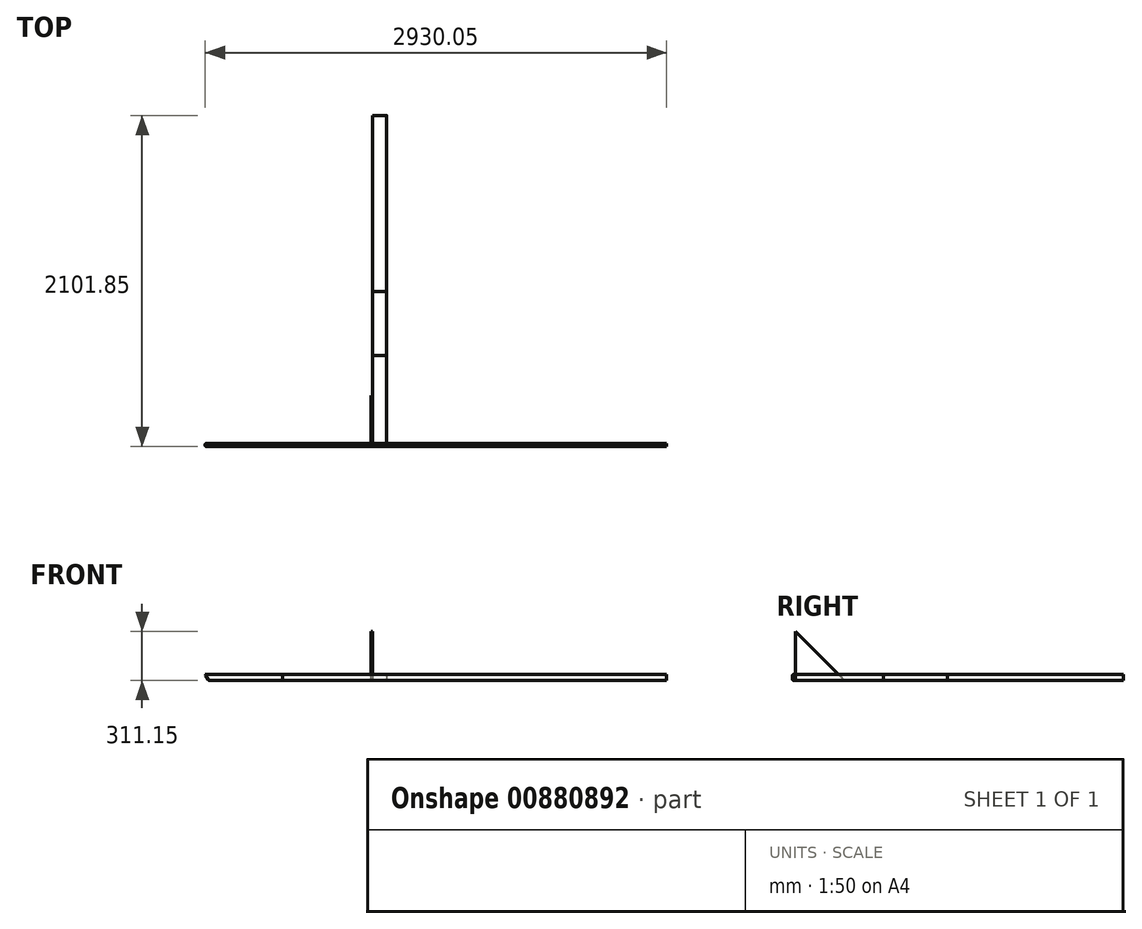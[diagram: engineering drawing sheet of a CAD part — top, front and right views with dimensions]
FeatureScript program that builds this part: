
annotation { "Feature Type Name" : "Feature", "Feature Type Description" : "" }
export const myFeature = defineFeature(function(context is Context, id is Id, definition is map)
    precondition{}
    {
        {
            var Q0;
            Q0=qCreatedBy(makeId("Top.planeOp"),FACE);
            var sketch = newSketch(context, id + "F0", { "sketchPlane" : qUnion([Q0])});
            skLineSegment(sketch, "E0", {"start": v(-1219.2, -1219.2) * mm, "end": v(0, 0) * mm});
            skLineSegment(sketch, "E1", {"start": v(0, 0) * mm, "end": v(1219.2, -1219.2) * mm});
            skLineSegment(sketch, "E2", {"start": v(1219.2, -1219.2) * mm, "end": v(-1219.2, -1219.2) * mm});
            skLineSegment(sketch, "E3", {"start": v(-1219.2, -1219.2) * mm, "end": v(-1219.2, -1238.25) * mm});
            skLineSegment(sketch, "E4", {"start": v(-1219.2, -1238.25) * mm, "end": v(1219.2, -1238.25) * mm});
            skLineSegment(sketch, "E5", {"start": v(1219.2, -1238.25) * mm, "end": v(1219.2, -1219.2) * mm});
            skLineSegment(sketch, "E6.bottom", {"start": v(-558.8, -1219.2) * mm, "end": v(-647.7, -1219.2) * mm});
            skLineSegment(sketch, "E6.top", {"start": v(-558.8, -660.4) * mm, "end": v(-647.7, -660.4) * mm});
            skLineSegment(sketch, "E6.left", {"start": v(-558.8, -1219.2) * mm, "end": v(-558.8, -660.4) * mm});
            skLineSegment(sketch, "E6.right", {"start": v(-647.7, -1219.2) * mm, "end": v(-647.7, -660.4) * mm});
            skLineSegment(sketch, "E7.bottom", {"start": v(558.8, -1219.2) * mm, "end": v(647.7, -1219.2) * mm});
            skLineSegment(sketch, "E7.top", {"start": v(558.8, -660.4) * mm, "end": v(647.7, -660.4) * mm});
            skLineSegment(sketch, "E7.left", {"start": v(558.8, -1219.2) * mm, "end": v(558.8, -660.4) * mm});
            skLineSegment(sketch, "E7.right", {"start": v(647.7, -1219.2) * mm, "end": v(647.7, -660.4) * mm});
            skLineSegment(sketch, "E8", {"start": v(-558.8, -660.4) * mm, "end": v(558.8, -660.4) * mm});
            skLineSegment(sketch, "E9", {"start": v(0, -660.4) * mm, "end": v(0, 0) * mm});
            skSolve(sketch);
        }
        {
            var Q0;
            {var subQ5=sQuery(id+"F0.wireOp",EDGE,"E3");Q0=makeQuery(id+"F0.imprint","IMPRINT",FACE,{"disambiguationData":[TD([[makeQuery(id+"F0.imprint","IMPRINT",EDGE,{"derivedFrom":subQ5}),1.0]])]});}
            extrude(context, id + "F1", {"entities" : qUnion([Q0]), "depth" : 38.1 * mm, "offsetDistance" : 25.4 * mm});
        }
        {
            var Q0;
            Q0=makeQuery(id+"F1.opExtrude","CAP_EDGE",EDGE,{"disambiguationData":[OSD([sQuery(id+"F0.wireOp",EDGE,"E4")])],"isStart":false});
            var Q1;
            Q1=makeQuery(id+"F1.opExtrude","CAP_EDGE",EDGE,{"disambiguationData":[OSD([sQuery(id+"F0.wireOp",EDGE,"E2")])],"isStart":false});
            var Q2;
            Q2=makeQuery(id+"F1.opExtrude","CAP_EDGE",EDGE,{"disambiguationData":[OSD([sQuery(id+"F0.wireOp",EDGE,"E4")])],"isStart":true});
            var Q3;
            Q3=makeQuery(id+"F1.opExtrude","CAP_EDGE",EDGE,{"disambiguationData":[OSD([sQuery(id+"F0.wireOp",EDGE,"E2")])],"isStart":true});
            fillet(context, id + "F2", {"entities" : qUnion([Q0, Q1, Q2, Q3]), "radius" : 6.35 * mm, "tangentPropagation" : true, "allowEdgeOverflow" : false});
        }
        {
            var Q0;
            Q0=makeQuery(id+"F1.opExtrude","SWEPT_FACE",FACE,{"disambiguationData":[OSD([sQuery(id+"F0.wireOp",EDGE,"E4")])]});
            var sketch = newSketch(context, id + "F3", { "sketchPlane" : qUnion([Q0])});
            skLineSegment(sketch, "E10", {"start": v(1173.07, 38.1) * mm, "end": v(1195.07, 0) * mm});
            skLineSegment(sketch, "E11", {"start": v(1195.07, 0) * mm, "end": v(703.42, 0) * mm});
            skLineSegment(sketch, "E12", {"start": v(703.42, 0) * mm, "end": v(703.42, 38.1) * mm});
            skLineSegment(sketch, "E13", {"start": v(703.42, 38.1) * mm, "end": v(211.76, 38.1) * mm});
            skLineSegment(sketch, "E14", {"start": v(211.76, 38.1) * mm, "end": v(233.76, 0) * mm});
            skLineSegment(sketch, "E15", {"start": v(233.76, 0) * mm, "end": v(-257.9, 0) * mm});
            skLineSegment(sketch, "E16", {"start": v(-257.9, 0) * mm, "end": v(-257.9, 38.1) * mm});
            skLineSegment(sketch, "E17", {"start": v(-257.9, 38.1) * mm, "end": v(-749.54, 38.1) * mm});
            skLineSegment(sketch, "E18", {"start": v(-749.54, 38.1) * mm, "end": v(-727.55, 0) * mm});
            skLineSegment(sketch, "E19", {"start": v(-727.55, 0) * mm, "end": v(-1219.2, 0) * mm});
            skLineSegment(sketch, "E20", {"start": v(-1219.2, 0) * mm, "end": v(-1219.2, 38.1) * mm});
            skLineSegment(sketch, "E21", {"start": v(-1219.2, 38.1) * mm, "end": v(-1710.85, 38.1) * mm});
            skLineSegment(sketch, "E22", {"start": v(-1710.85, 38.1) * mm, "end": v(-1688.86, 0) * mm});
            skLineSegment(sketch, "E23", {"start": v(-1688.86, 0) * mm, "end": v(-1710.85, 0) * mm});
            skLineSegment(sketch, "E24", {"start": v(-1710.85, 0) * mm, "end": v(-1710.85, 38.1) * mm});
            skSolve(sketch);
        }
        {
            var Q0;
            Q0=makeQuery(id+"F1.opExtrude","SWEPT_FACE",FACE,{"disambiguationData":[OSD([sQuery(id+"F0.wireOp",EDGE,"E3")])]});
            var Q1;
            Q1=sQuery(id+"F3.wireOp",VERTEX,"E21.end");
            extrude(context, id + "F4", {"entities" : qUnion([Q0]), "endBound" : BoundingType.UP_TO_VERTEX, "depth" : 482.6 * mm, "endBoundEntityVertex" : qUnion([Q1]), "offsetDistance" : 25.4 * mm});
        }
        {
            var Q0;
            Q0=makeQuery(id+"F3.imprint","IMPRINT",FACE,{"disambiguationData":[TD([[makeQuery(id+"F3.imprint","IMPRINT",EDGE,{"derivedFrom":sQuery(id+"F3.wireOp",EDGE,"E22")}),-1.0]])]});
            extrude(context, id + "F5", {"entities" : qUnion([Q0]), "operationType" : NewBodyOperationType.REMOVE, "endBound" : BoundingType.THROUGH_ALL, "oppositeDirection" : true, "depth" : 25.4 * mm, "offsetDistance" : 25.4 * mm});
        }
        {
            var Q0;
            Q0=makeQuery(id+"F0.imprint","IMPRINT",FACE,{"disambiguationData":[TD([[makeQuery(id+"F0.imprint","IMPRINT",EDGE,{"derivedFrom":sQuery(id+"F0.wireOp",EDGE,"E6.top")}),1.0]])]});
            extrude(context, id + "F6", {"entities" : qUnion([Q0]), "depth" : 38.1 * mm, "offsetDistance" : 25.4 * mm});
        }
        {
            var Q0;
            Q0=makeQuery(id+"F6.opExtrude","CAP_EDGE",EDGE,{"disambiguationData":[OSD([sQuery(id+"F0.wireOp",EDGE,"E6.right")])],"isStart":false});
            var Q1;
            Q1=makeQuery(id+"F6.opExtrude","CAP_EDGE",EDGE,{"disambiguationData":[OSD([sQuery(id+"F0.wireOp",EDGE,"E6.right")])],"isStart":true});
            var Q2;
            Q2=makeQuery(id+"F6.opExtrude","CAP_EDGE",EDGE,{"disambiguationData":[OSD([sQuery(id+"F0.wireOp",EDGE,"E6.left")])],"isStart":false});
            var Q3;
            Q3=makeQuery(id+"F6.opExtrude","CAP_EDGE",EDGE,{"disambiguationData":[OSD([sQuery(id+"F0.wireOp",EDGE,"E6.left")])],"isStart":true});
            var Q4;
            Q4=makeQuery(id+"F5.boolean.opBoolean","COPY",EDGE,{"derivedFrom":makeQuery(id+"F5.opExtrude","CAP_EDGE",EDGE,{"disambiguationData":[OSD([sQuery(id+"F3.wireOp",EDGE,"E22")])],"isStart":true})});
            fillet(context, id + "F7", {"entities" : qUnion([Q0, Q1, Q2, Q3, Q4]), "radius" : 6.35 * mm, "tangentPropagation" : true, "allowEdgeOverflow" : false});
        }
        {
            var Q0;
            Q0=makeQuery(id+"F6.opExtrude","SWEPT_FACE",FACE,{"disambiguationData":[OSD([sQuery(id+"F0.wireOp",EDGE,"E6.top")])]});
            extrude(context, id + "F8", {"entities" : qUnion([Q0]), "depth" : 406.4 * mm, "offsetDistance" : 25.4 * mm});
        }
        {
            var Q0;
            Q0=makeQuery(id+"F6.opExtrude","SWEPT_FACE",FACE,{"disambiguationData":[OSD([sQuery(id+"F0.wireOp",EDGE,"E6.right")])]});
            var sketch = newSketch(context, id + "F9", { "sketchPlane" : qUnion([Q0])});
            skLineSegment(sketch, "E25", {"start": v(914.4, 6.35) * mm, "end": v(1219.2, 6.35) * mm});
            skLineSegment(sketch, "E26", {"start": v(1219.2, 6.35) * mm, "end": v(1219.2, 311.15) * mm});
            skLineSegment(sketch, "E27", {"start": v(1219.2, 311.15) * mm, "end": v(914.4, 6.35) * mm});
            skSolve(sketch);
        }
        {
            var Q0;
            {var subQ0=sQuery(id+"F9.wireOp",EDGE,"E26");var subQ4=sQuery(id+"F9.wireOp",EDGE,"E27");var subQ5=makeQuery(id+"F9.imprint","INTERSECT",VERTEX,{"derivedFrom":[subQ0,subQ4]});Q0=makeQuery(id+"F9.imprint","IMPRINT",FACE,{"disambiguationData":[TD([[makeQuery(id+"F9.imprint","IMPRINT",EDGE,{"disambiguationData":[TD([[subQ5,1.0]])],"derivedFrom":subQ0}),1.0]])]});}
            var Q1;
            {var subQ0=sQuery(id+"F9.wireOp",EDGE,"E25");Q1=makeQuery(id+"F9.imprint","IMPRINT",FACE,{"disambiguationData":[TD([[makeQuery(id+"F9.imprint","IMPRINT",EDGE,{"derivedFrom":subQ0}),1.0]])]});}
            extrude(context, id + "F10", {"entities" : qUnion([Q0, Q1]), "depth" : 9.52 * mm, "offsetDistance" : 25.4 * mm});
        }
        {
            var Q0;
            Q0=makeQuery(id+"F8.opExtrude","CAP_FACE",FACE,{"disambiguationData":[OSD([sQuery(id+"F0.wireOp",EDGE,"E6.top")])],"isStart":false});
            extrude(context, id + "F11", {"entities" : qUnion([Q0]), "depth" : 1117.6 * mm, "offsetDistance" : 25.4 * mm});
        }
    });
